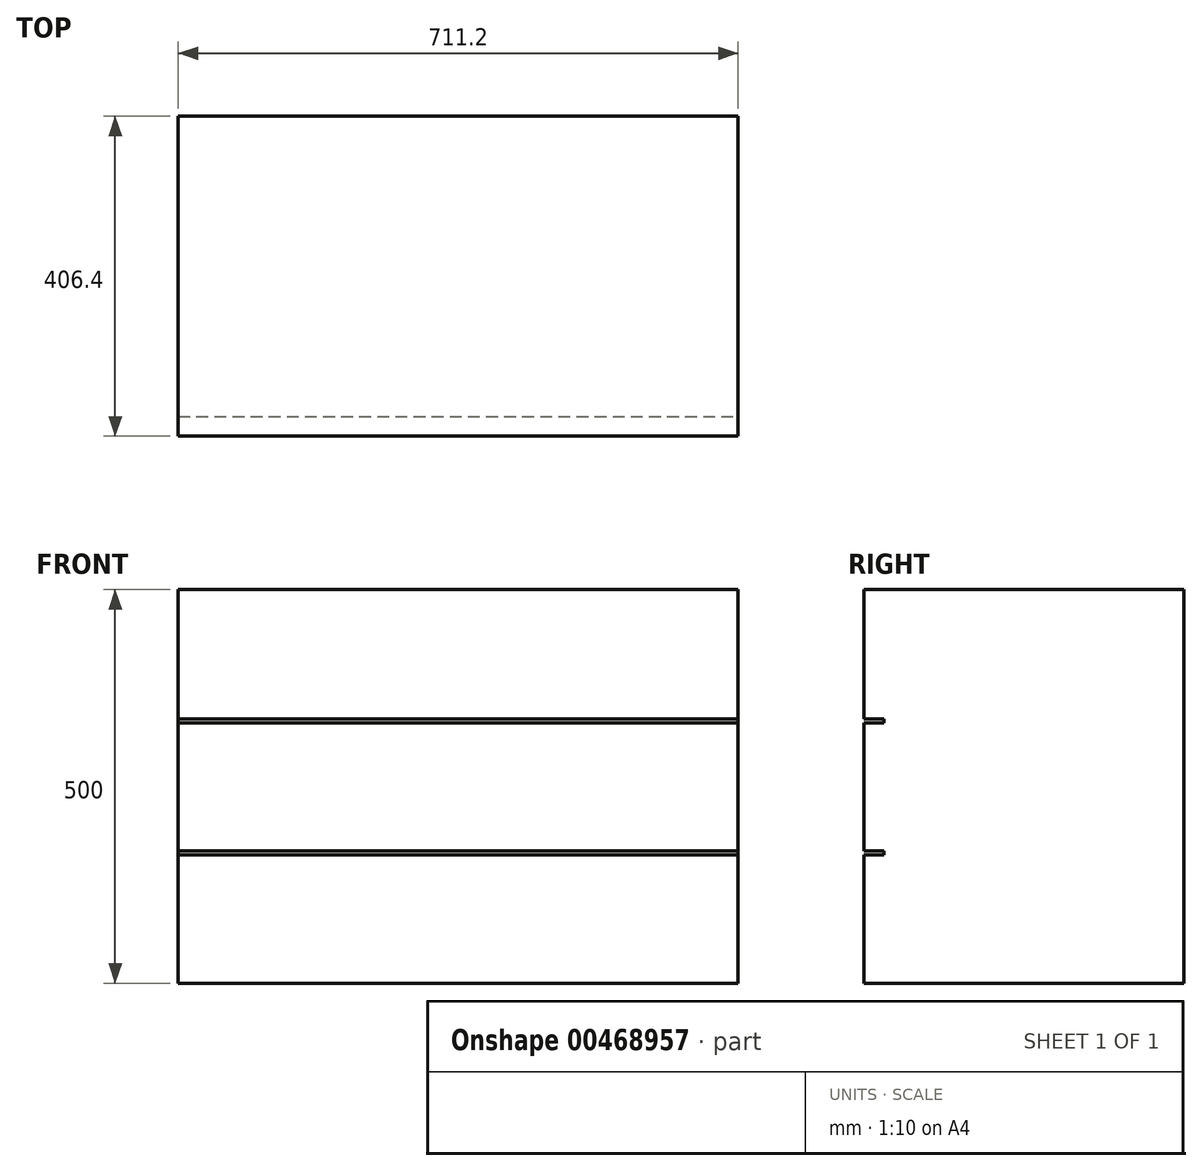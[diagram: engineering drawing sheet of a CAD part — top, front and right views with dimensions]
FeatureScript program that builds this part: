
annotation { "Feature Type Name" : "Feature", "Feature Type Description" : "" }
export const myFeature = defineFeature(function(context is Context, id is Id, definition is map)
    precondition{}
    {
        {
            var Q0;
            Q0=qCreatedBy(makeId("Top.planeOp"),FACE);
            var sketch = newSketch(context, id + "F0", { "sketchPlane" : qUnion([Q0])});
            skLineSegment(sketch, "E0.bottom", {"start": v(-355.6, 203.2) * mm, "end": v(355.6, 203.2) * mm});
            skLineSegment(sketch, "E0.top", {"start": v(-355.6, -203.2) * mm, "end": v(355.6, -203.2) * mm});
            skLineSegment(sketch, "E0.left", {"start": v(-355.6, 203.2) * mm, "end": v(-355.6, -203.2) * mm});
            skLineSegment(sketch, "E0.right", {"start": v(355.6, 203.2) * mm, "end": v(355.6, -203.2) * mm});
            skPoint(sketch, "E0.middle", {"position": v(0, 0) * mm});
            skSolve(sketch);
        }
        {
            var Q0;
            Q0=makeQuery(id+"F0.imprint","IMPRINT",FACE,{"disambiguationData":[TD([[makeQuery(id+"F0.imprint","IMPRINT",EDGE,{"derivedFrom":sQuery(id+"F0.wireOp",EDGE,"E0.bottom")}),-1.0]])]});
            extrude(context, id + "F1", {"entities" : qUnion([Q0]), "depth" : 500 * mm});
        }
        {
            var Q0;
            Q0=makeQuery(id+"F1.opExtrude","SWEPT_FACE",FACE,{"disambiguationData":[OSD([sQuery(id+"F0.wireOp",EDGE,"E0.top")])]});
            var sketch = newSketch(context, id + "F2", { "sketchPlane" : qUnion([Q0])});
            skLineSegment(sketch, "E1", {"start": v(-355.6, 336) * mm, "end": v(355.6, 336) * mm});
            skLineSegment(sketch, "E2", {"start": v(355.6, 336) * mm, "end": v(355.6, 331) * mm});
            skLineSegment(sketch, "E3", {"start": v(355.6, 331) * mm, "end": v(-355.6, 331) * mm});
            skLineSegment(sketch, "E4", {"start": v(-355.6, 331) * mm, "end": v(-355.6, 336) * mm});
            skLineSegment(sketch, "E5", {"start": v(-355.6, 168) * mm, "end": v(355.6, 168) * mm});
            skLineSegment(sketch, "E6", {"start": v(355.6, 168) * mm, "end": v(355.6, 163) * mm});
            skLineSegment(sketch, "E7", {"start": v(355.6, 163) * mm, "end": v(-355.6, 163) * mm});
            skLineSegment(sketch, "E8", {"start": v(-355.6, 163) * mm, "end": v(-355.6, 168) * mm});
            skSolve(sketch);
        }
        {
            var Q0;
            Q0 = qSketchRegion(id + "F2", true);
            extrude(context, id + "F3", {"entities" : qUnion([Q0]), "operationType" : NewBodyOperationType.REMOVE, "oppositeDirection" : true, "depth" : 25 * mm});
        }
    });
